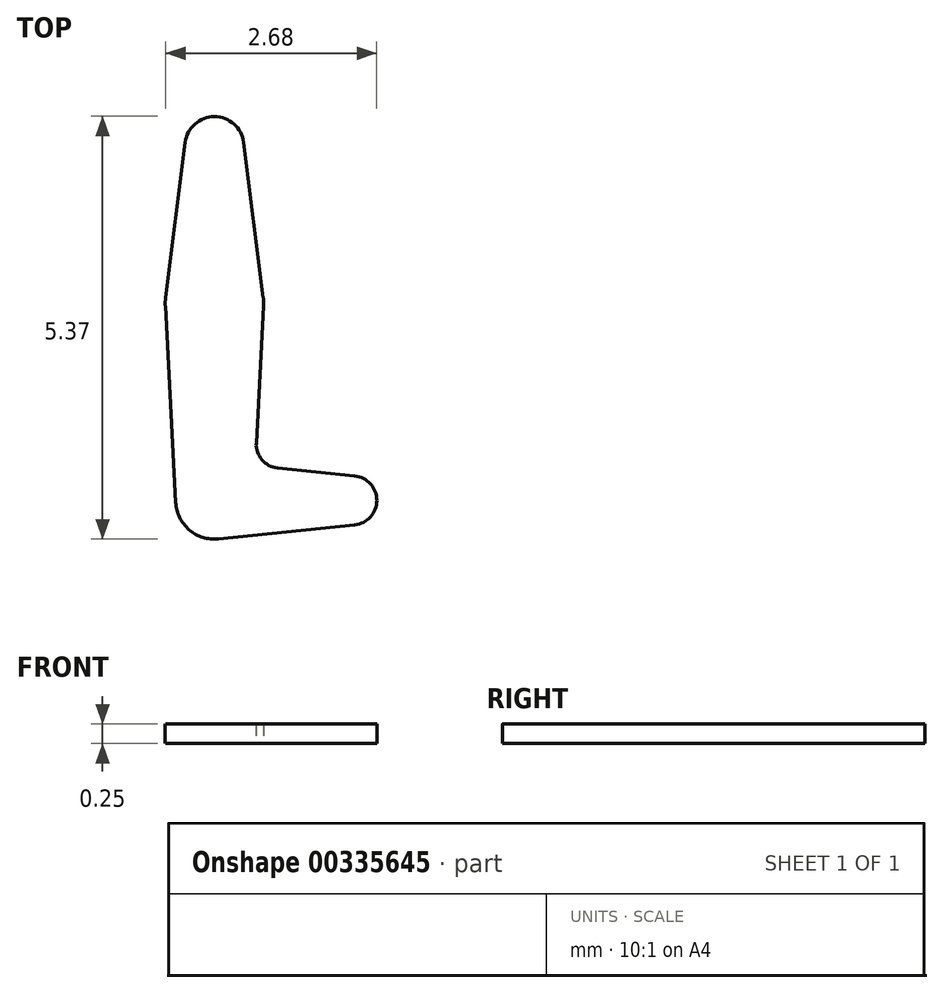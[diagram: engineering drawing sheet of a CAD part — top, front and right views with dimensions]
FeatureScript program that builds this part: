
annotation { "Feature Type Name" : "Feature", "Feature Type Description" : "" }
export const myFeature = defineFeature(function(context is Context, id is Id, definition is map)
    precondition{}
    {
        {
            var Q0;
            Q0=qCreatedBy(makeId("Top.planeOp"),FACE);
            var sketch = newSketch(context, id + "F0", { "sketchPlane" : qUnion([Q0])});
            skLineSegment(sketch, "E0", {"start": v(0, 0) * mm, "end": v(0, 4.5) * mm, "construction": true});
            skCircle(sketch, "E1", {"center": v(0, 0) * mm, "radius": 0.5 * mm});
            skCircle(sketch, "E2", {"center": v(0, 4.5) * mm, "radius": 0.38 * mm});
            skCircle(sketch, "E3", {"center": v(0, 2.5) * mm, "radius": 0.62 * mm});
            skLineSegment(sketch, "E4", {"start": v(0, 0) * mm, "end": v(1.75, 0) * mm, "construction": true});
            skCircle(sketch, "E5", {"center": v(1.75, 0) * mm, "radius": 0.31 * mm});
            skLineSegment(sketch, "E6", {"start": v(-0.37, 4.55) * mm, "end": v(-0.62, 2.58) * mm});
            skLineSegment(sketch, "E7", {"start": v(0.37, 4.55) * mm, "end": v(0.62, 2.58) * mm});
            skLineSegment(sketch, "E8", {"start": v(-0.62, 2.47) * mm, "end": v(-0.5, -0.03) * mm});
            skLineSegment(sketch, "E9", {"start": v(0.53, 0.73) * mm, "end": v(0.62, 2.47) * mm});
            skLineSegment(sketch, "E10", {"start": v(0.8, 0.41) * mm, "end": v(1.78, 0.31) * mm});
            skLineSegment(sketch, "E11", {"start": v(0.05, -0.49) * mm, "end": v(1.78, -0.31) * mm});
            skArc(sketch, "E12.filletArc", {"start": v(0.53, 0.73) * mm, "mid": v(0.6, 0.52) * mm, "end": v(0.8, 0.41) * mm});
            skSolve(sketch);
        }
        {
            var Q0;
            {var subQ0=sQuery(id+"F0.wireOp",EDGE,"E2");var subQ1=makeQuery(id+"F0.imprint","INTERSECT",VERTEX,{"derivedFrom":[subQ0,sQuery(id+"F0.wireOp",EDGE,"E6")]});Q0=makeQuery(id+"F0.imprint","IMPRINT",FACE,{"disambiguationData":[TD([[makeQuery(id+"F0.imprint","IMPRINT",EDGE,{"disambiguationData":[TD([[subQ1,1.0]])],"derivedFrom":subQ0}),1.0]])]});}
            var Q1;
            {var subQ0=sQuery(id+"F0.wireOp",EDGE,"E3");var subQ1=makeQuery(id+"F0.imprint","INTERSECT",VERTEX,{"derivedFrom":[subQ0,sQuery(id+"F0.wireOp",EDGE,"E6")]});Q1=makeQuery(id+"F0.imprint","IMPRINT",FACE,{"disambiguationData":[TD([[makeQuery(id+"F0.imprint","IMPRINT",EDGE,{"disambiguationData":[TD([[subQ1,1.0]])],"derivedFrom":subQ0}),1.0]])]});}
            var Q2;
            {var subQ0=sQuery(id+"F0.wireOp",EDGE,"E6");Q2=makeQuery(id+"F0.imprint","IMPRINT",FACE,{"disambiguationData":[TD([[makeQuery(id+"F0.imprint","IMPRINT",EDGE,{"derivedFrom":subQ0}),1.0]])]});}
            var Q3;
            {var subQ0=sQuery(id+"F0.wireOp",EDGE,"E8");Q3=makeQuery(id+"F0.imprint","IMPRINT",FACE,{"disambiguationData":[TD([[makeQuery(id+"F0.imprint","IMPRINT",EDGE,{"derivedFrom":subQ0}),1.0]])]});}
            var Q4;
            {var subQ0=sQuery(id+"F0.wireOp",EDGE,"E5");var subQ1=makeQuery(id+"F0.imprint","INTERSECT",VERTEX,{"derivedFrom":[subQ0,sQuery(id+"F0.wireOp",EDGE,"E10")]});Q4=makeQuery(id+"F0.imprint","IMPRINT",FACE,{"disambiguationData":[TD([[makeQuery(id+"F0.imprint","IMPRINT",EDGE,{"disambiguationData":[TD([[subQ1,-1.0]])],"derivedFrom":subQ0}),1.0]])]});}
            var Q5;
            {var subQ0=sQuery(id+"F0.wireOp",EDGE,"E1");var subQ1=makeQuery(id+"F0.imprint","INTERSECT",VERTEX,{"derivedFrom":[subQ0,sQuery(id+"F0.wireOp",EDGE,"E8")]});Q5=makeQuery(id+"F0.imprint","IMPRINT",FACE,{"disambiguationData":[TD([[makeQuery(id+"F0.imprint","IMPRINT",EDGE,{"disambiguationData":[TD([[subQ1,-1.0]])],"derivedFrom":subQ0}),1.0]])]});}
            extrude(context, id + "F1", {"entities" : qUnion([Q0, Q1, Q2, Q3, Q4, Q5]), "depth" : 0.25 * mm});
        }
    });
